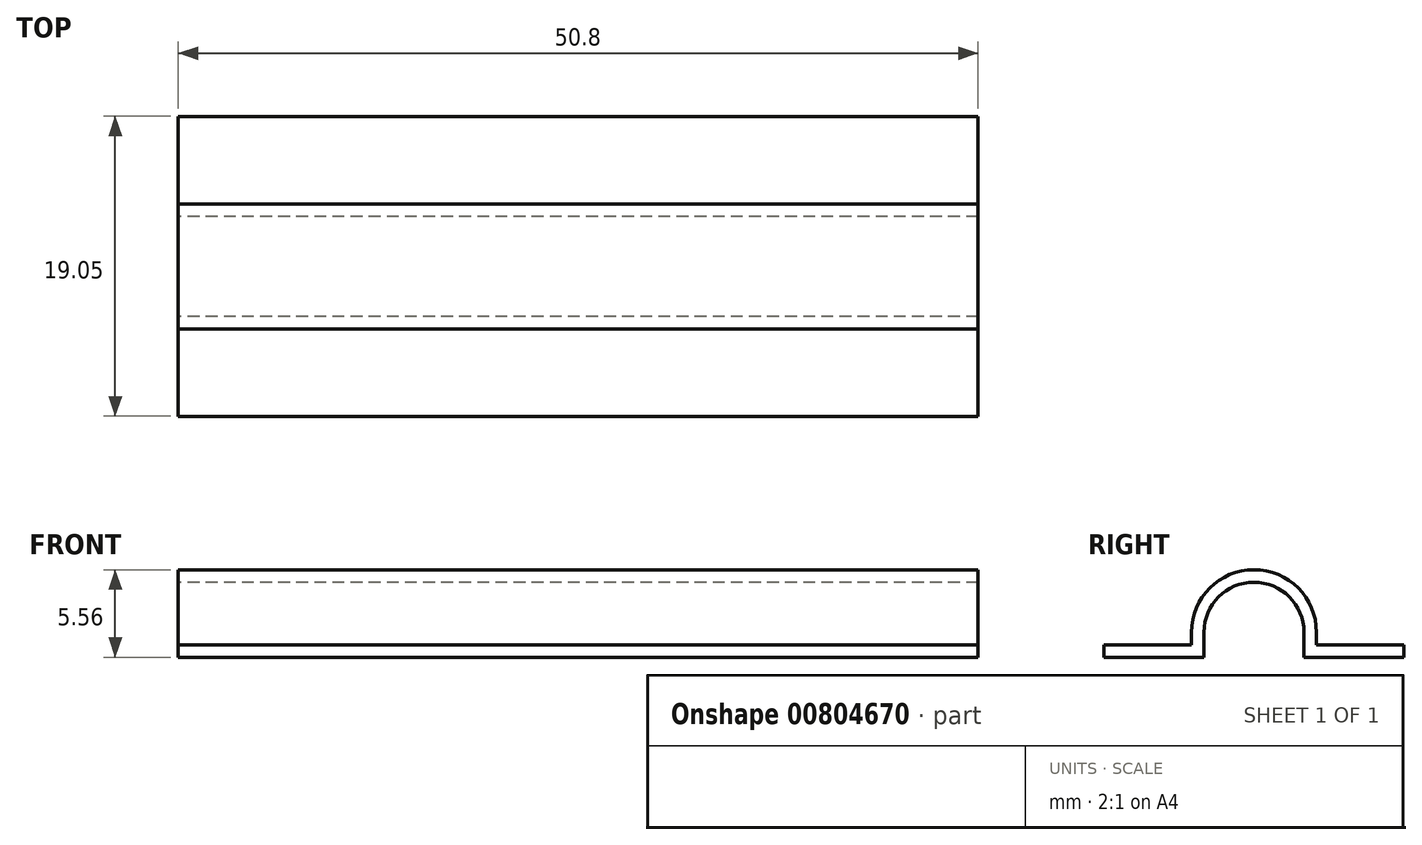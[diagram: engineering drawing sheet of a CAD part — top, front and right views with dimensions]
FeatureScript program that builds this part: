
annotation { "Feature Type Name" : "Feature", "Feature Type Description" : "" }
export const myFeature = defineFeature(function(context is Context, id is Id, definition is map)
    precondition{}
    {
        {
            var Q0;
            Q0=qCreatedBy(makeId("Right.planeOp"),FACE);
            var sketch = newSketch(context, id + "F0", { "sketchPlane" : qUnion([Q0])});
            skLineSegment(sketch, "E0", {"start": v(-2.1, 0) * mm, "end": v(-8.45, 0) * mm});
            skLineSegment(sketch, "E1", {"start": v(-2.1, 0) * mm, "end": v(-2.1, 1.59) * mm});
            skArc(sketch, "E2", {"start": v(4.25, 1.59) * mm, "mid": v(1.07, 4.76) * mm, "end": v(-2.1, 1.59) * mm});
            skLineSegment(sketch, "E3", {"start": v(4.25, 1.59) * mm, "end": v(4.25, 0) * mm});
            skLineSegment(sketch, "E4", {"start": v(4.25, 0) * mm, "end": v(10.6, 0) * mm});
            skLineSegment(sketch, "E5.0", {"start": v(-2.9, 0.8) * mm, "end": v(-8.45, 0.8) * mm});
            skLineSegment(sketch, "E5.1", {"start": v(5.04, 0.8) * mm, "end": v(10.6, 0.8) * mm});
            skLineSegment(sketch, "E5.2", {"start": v(5.04, 1.59) * mm, "end": v(5.04, 0.8) * mm});
            skArc(sketch, "E5.3", {"start": v(5.04, 1.59) * mm, "mid": v(1.07, 5.56) * mm, "end": v(-2.9, 1.59) * mm});
            skLineSegment(sketch, "E5.4", {"start": v(-2.9, 0.8) * mm, "end": v(-2.9, 1.59) * mm});
            skLineSegment(sketch, "E6", {"start": v(-8.45, 0.8) * mm, "end": v(-8.45, 0) * mm});
            skLineSegment(sketch, "E7", {"start": v(10.6, 0.8) * mm, "end": v(10.6, 0) * mm});
            skSolve(sketch);
        }
        {
            var Q0;
            Q0=makeQuery(id+"F0.imprint","IMPRINT",FACE,{"disambiguationData":[TD([[makeQuery(id+"F0.imprint","IMPRINT",EDGE,{"derivedFrom":sQuery(id+"F0.wireOp",EDGE,"E0")}),-1.0]])]});
            extrude(context, id + "F1", {"entities" : qUnion([Q0]), "depth" : 50.8 * mm, "offsetDistance" : 25.4 * mm});
        }
    });
